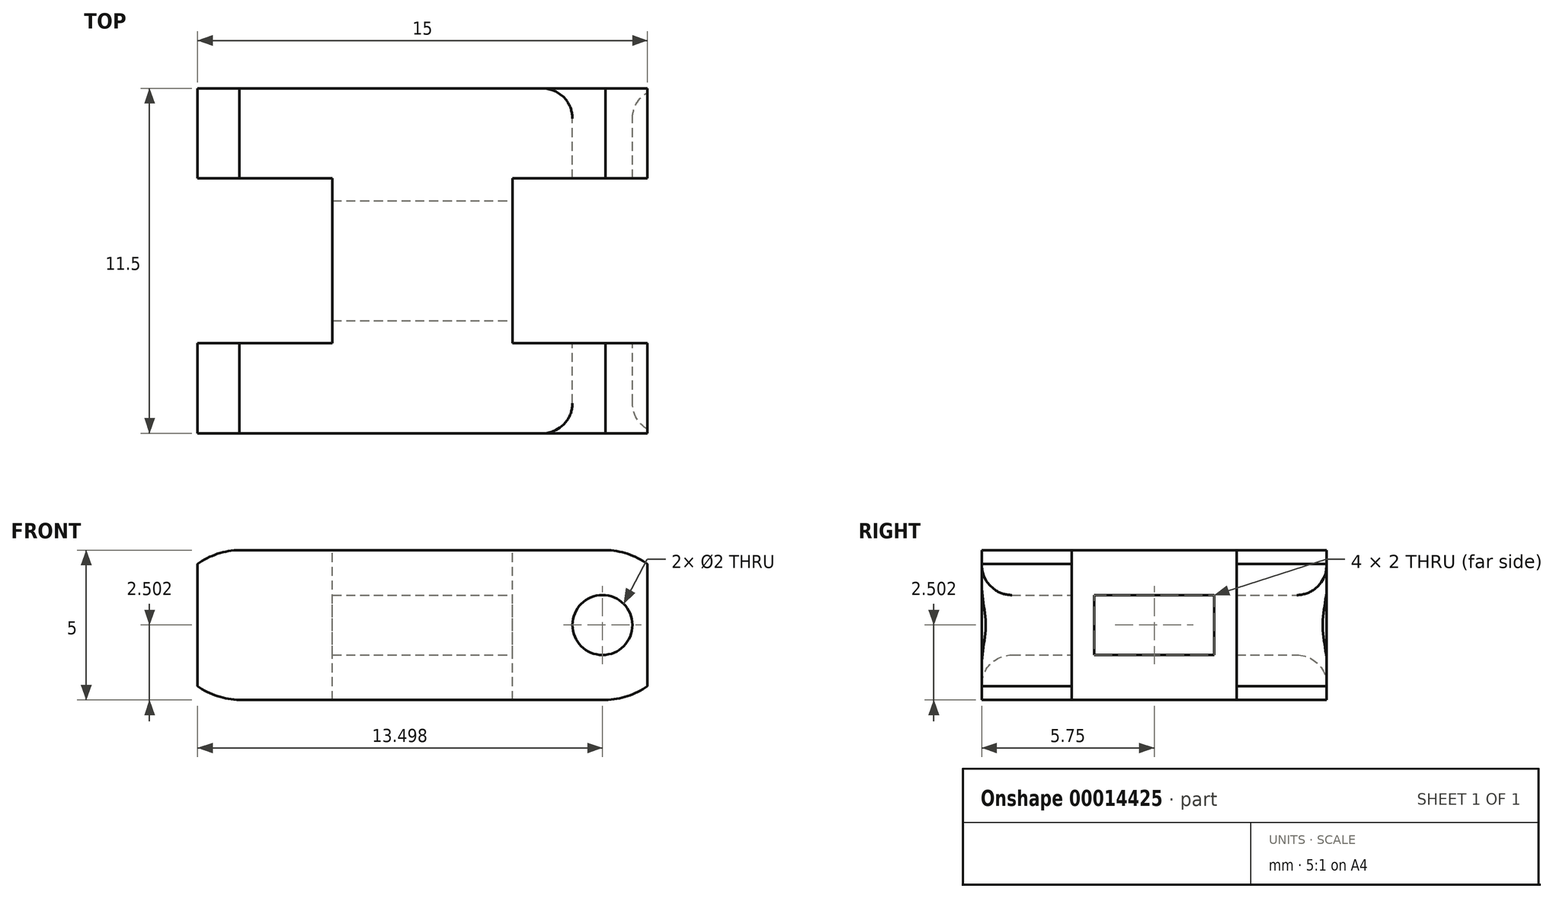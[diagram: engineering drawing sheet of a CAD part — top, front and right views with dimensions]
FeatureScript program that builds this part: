
annotation { "Feature Type Name" : "Feature", "Feature Type Description" : "" }
export const myFeature = defineFeature(function(context is Context, id is Id, definition is map)
    precondition{}
    {
        {
            var Q0;
            Q0=qCreatedBy(makeId("Front.planeOp"),FACE);
            var sketch = newSketch(context, id + "F0", { "sketchPlane" : qUnion([Q0])});
            skLineSegment(sketch, "E0.bottom", {"start": v(28.09, 13.2) * mm, "end": v(43.09, 13.2) * mm});
            skLineSegment(sketch, "E0.top", {"start": v(28.09, 8.2) * mm, "end": v(43.09, 8.2) * mm});
            skLineSegment(sketch, "E0.left", {"start": v(28.09, 13.2) * mm, "end": v(28.09, 8.2) * mm});
            skLineSegment(sketch, "E0.right", {"start": v(43.09, 13.2) * mm, "end": v(43.09, 8.2) * mm});
            skLineSegment(sketch, "E1", {"start": v(35.59, 8.2) * mm, "end": v(35.59, 13.2) * mm, "construction": true});
            skPoint(sketch, "E2", {"position": v(31.09, 13.2) * mm});
            skLineSegment(sketch, "E3", {"start": v(28.09, 8.2) * mm, "end": v(31.09, 13.2) * mm, "construction": true});
            skLineSegment(sketch, "E4", {"start": v(31.09, 13.2) * mm, "end": v(31.09, 8.2) * mm, "construction": true});
            skLineSegment(sketch, "E5", {"start": v(31.09, 8.2) * mm, "end": v(28.09, 13.2) * mm, "construction": true});
            skCircle(sketch, "E6", {"center": v(29.59, 10.7) * mm, "radius": 1 * mm});
            skLineSegment(sketch, "E7", {"start": v(29.59, 13.2) * mm, "end": v(29.59, 8.2) * mm, "construction": true});
            skLineSegment(sketch, "E8", {"start": v(28.09, 10.7) * mm, "end": v(31.09, 10.7) * mm, "construction": true});
            skArc(sketch, "E9", {"start": v(29.59, 13.2) * mm, "mid": v(27.04, 10.7) * mm, "end": v(29.59, 8.2) * mm});
            skCircle(sketch, "E10.0.MirrorC", {"center": v(41.59, 10.7) * mm, "radius": 1 * mm});
            skArc(sketch, "E11.0.MirrorCS", {"start": v(41.59, 13.2) * mm, "mid": v(44.14, 10.7) * mm, "end": v(41.59, 8.2) * mm});
            skSolve(sketch);
        }
        {
            var Q0;
            {var subQ5=sQuery(id+"F0.wireOp",EDGE,"E0.right");Q0=makeQuery(id+"F0.imprint","IMPRINT",FACE,{"disambiguationData":[TD([[makeQuery(id+"F0.imprint","IMPRINT",EDGE,{"derivedFrom":subQ5}),-1.0]])]});}
            var Q1;
            Q1=makeQuery(id+"F0.imprint","IMPRINT",FACE,{"disambiguationData":[TD([[makeQuery(id+"F0.imprint","IMPRINT",EDGE,{"derivedFrom":sQuery(id+"F0.wireOp",EDGE,"E6")}),-1.0]])]});
            var Q2;
            {var subQ5=sQuery(id+"F0.wireOp",EDGE,"E0.left");Q2=makeQuery(id+"F0.imprint","IMPRINT",FACE,{"disambiguationData":[TD([[makeQuery(id+"F0.imprint","IMPRINT",EDGE,{"derivedFrom":subQ5}),1.0]])]});}
            var Q3;
            Q3=makeQuery(id+"F0.imprint","IMPRINT",FACE,{"disambiguationData":[TD([[makeQuery(id+"F0.imprint","IMPRINT",EDGE,{"derivedFrom":sQuery(id+"F0.wireOp",EDGE,"E6")}),1.0]])]});
            var Q4;
            Q4=makeQuery(id+"F0.imprint","IMPRINT",FACE,{"disambiguationData":[TD([[makeQuery(id+"F0.imprint","IMPRINT",EDGE,{"derivedFrom":sQuery(id+"F0.wireOp",EDGE,"E10.0.MirrorC")}),-1.0]])]});
            extrude(context, id + "F1", {"entities" : qUnion([Q0, Q1, Q2, Q3, Q4]), "depth" : 9.5 * mm});
        }
        {
            var Q0;
            Q0=makeQuery(id+"F1.opExtrude","SWEPT_FACE",FACE,{"disambiguationData":[OSD([sQuery(id+"F0.wireOp",EDGE,"E0.bottom")])]});
            var sketch = newSketch(context, id + "F2", { "sketchPlane" : qUnion([Q0])});
            skLineSegment(sketch, "E12", {"start": v(35.59, 0) * mm, "end": v(35.59, -9.5) * mm, "construction": true});
            skLineSegment(sketch, "E13", {"start": v(28.09, -4.75) * mm, "end": v(43.09, -4.75) * mm, "construction": true});
            skPoint(sketch, "E14", {"position": v(32.59, 0) * mm});
            skLineSegment(sketch, "E15", {"start": v(32.59, 0) * mm, "end": v(32.59, -9.5) * mm, "construction": true});
            skPoint(sketch, "E16", {"position": v(28.09, -2) * mm});
            skLineSegment(sketch, "E17", {"start": v(28.09, -2) * mm, "end": v(32.59, -2) * mm});
            skLineSegment(sketch, "E18.0.MirrorCS", {"start": v(28.09, -7.5) * mm, "end": v(32.59, -7.5) * mm});
            skLineSegment(sketch, "E19", {"start": v(32.59, -7.5) * mm, "end": v(32.59, -2) * mm});
            skLineSegment(sketch, "E20", {"start": v(28.09, -2) * mm, "end": v(28.09, -7.5) * mm});
            skLineSegment(sketch, "E21.MirrorCS", {"start": v(38.59, -7.5) * mm, "end": v(38.59, -2) * mm});
            skLineSegment(sketch, "E22.MirrorCS", {"start": v(43.09, -2) * mm, "end": v(38.59, -2) * mm});
            skLineSegment(sketch, "E23.MirrorCS", {"start": v(43.09, -2) * mm, "end": v(43.09, -7.5) * mm});
            skLineSegment(sketch, "E24.MirrorCS", {"start": v(43.09, -7.5) * mm, "end": v(38.59, -7.5) * mm});
            skSolve(sketch);
        }
        {
            var Q0;
            Q0=makeQuery(id+"F2.imprint","IMPRINT",FACE,{"disambiguationData":[TD([[makeQuery(id+"F2.imprint","IMPRINT",EDGE,{"derivedFrom":sQuery(id+"F2.wireOp",EDGE,"E17")}),-1.0]])]});
            var Q1;
            Q1=makeQuery(id+"F2.imprint","IMPRINT",FACE,{"disambiguationData":[TD([[makeQuery(id+"F2.imprint","IMPRINT",EDGE,{"derivedFrom":sQuery(id+"F2.wireOp",EDGE,"8c34fa15-d911-4d8d-b620-4605c3a337e2.0.MirrorCS")}),-1.0]])]});
            var Q2;
            Q2=makeQuery(id+"F2.imprint","IMPRINT",FACE,{"disambiguationData":[TD([[makeQuery(id+"F2.imprint","IMPRINT",EDGE,{"derivedFrom":sQuery(id+"F2.wireOp",EDGE,"E21.MirrorCS")}),-1.0]])]});
            extrude(context, id + "F3", {"entities" : qUnion([Q0, Q1, Q2]), "operationType" : NewBodyOperationType.REMOVE, "endBound" : BoundingType.THROUGH_ALL, "oppositeDirection" : true, "depth" : 25 * mm});
        }
        {
            var Q0;
            {var subQ5=sQuery(id+"F0.wireOp",EDGE,"E0.right");Q0=makeQuery(id+"F0.imprint","IMPRINT",FACE,{"disambiguationData":[TD([[makeQuery(id+"F0.imprint","IMPRINT",EDGE,{"derivedFrom":subQ5}),-1.0]])]});}
            var Q1;
            {var subQ5=sQuery(id+"F0.wireOp",EDGE,"E0.left");Q1=makeQuery(id+"F0.imprint","IMPRINT",FACE,{"disambiguationData":[TD([[makeQuery(id+"F0.imprint","IMPRINT",EDGE,{"derivedFrom":subQ5}),1.0]])]});}
            extrude(context, id + "F4", {"entities" : qUnion([Q0, Q1]), "operationType" : NewBodyOperationType.REMOVE, "endBound" : BoundingType.THROUGH_ALL, "depth" : 25 * mm});
        }
        {
            var Q0;
            Q0=makeQuery(id+"F0.imprint","IMPRINT",FACE,{"disambiguationData":[TD([[makeQuery(id+"F0.imprint","IMPRINT",EDGE,{"derivedFrom":sQuery(id+"F0.wireOp",EDGE,"E6")}),1.0]])]});
            var Q1;
            Q1=makeQuery(id+"F0.imprint","IMPRINT",FACE,{"disambiguationData":[TD([[makeQuery(id+"F0.imprint","IMPRINT",EDGE,{"derivedFrom":sQuery(id+"F0.wireOp",EDGE,"E10.0.MirrorC")}),-1.0]])]});
            extrude(context, id + "F5", {"entities" : qUnion([Q0, Q1]), "operationType" : NewBodyOperationType.ADD, "oppositeDirection" : true, "depth" : 1 * mm});
        }
        {
            var Q0;
            Q0=makeQuery(id+"F1.opExtrude","CAP_FACE",FACE,{"disambiguationData":[OSD([sQuery(id+"F0.wireOp",EDGE,"E0.bottom"),sQuery(id+"F0.wireOp",EDGE,"E0.top"),sQuery(id+"F0.wireOp",EDGE,"E0.left"),sQuery(id+"F0.wireOp",EDGE,"E0.right")])],"isStart":false});
            var sketch = newSketch(context, id + "F6", { "sketchPlane" : qUnion([Q0])});
            skLineSegment(sketch, "E25", {"start": v(35.59, 8.2) * mm, "end": v(35.59, 13.2) * mm, "construction": true});
            skPoint(sketch, "E26", {"position": v(31.09, 8.2) * mm});
            skPoint(sketch, "E27", {"position": v(28.09, 8.2) * mm});
            skLineSegment(sketch, "E28", {"start": v(31.09, 8.2) * mm, "end": v(31.09, 13.2) * mm, "construction": true});
            skLineSegment(sketch, "E29", {"start": v(31.09, 13.2) * mm, "end": v(28.09, 8.2) * mm, "construction": true});
            skPoint(sketch, "E30", {"position": v(28.09, 13.2) * mm});
            skLineSegment(sketch, "E31", {"start": v(28.09, 13.2) * mm, "end": v(28.09, 8.2) * mm, "construction": true});
            skLineSegment(sketch, "E32", {"start": v(31.09, 13.2) * mm, "end": v(28.09, 13.2) * mm, "construction": true});
            skLineSegment(sketch, "E33", {"start": v(28.09, 13.2) * mm, "end": v(31.09, 8.2) * mm, "construction": true});
            skCircle(sketch, "E34", {"center": v(29.59, 10.7) * mm, "radius": 1 * mm});
            skCircle(sketch, "E35.MirrorC", {"center": v(41.59, 10.7) * mm, "radius": 1 * mm});
            skPoint(sketch, "E36", {"position": v(35.59, 8.2) * mm});
            skCircle(sketch, "E37.MirrorC", {"center": v(41.59, 10.7) * mm, "radius": 1 * mm, "construction": true});
            skSolve(sketch);
        }
        {
            var Q0;
            Q0=makeQuery(id+"F6.imprint","IMPRINT",FACE,{"disambiguationData":[TD([[makeQuery(id+"F6.imprint","IMPRINT",EDGE,{"derivedFrom":sQuery(id+"F6.wireOp",EDGE,"E34")}),1.0]])]});
            var Q1;
            Q1=makeQuery(id+"F6.imprint","IMPRINT",FACE,{"disambiguationData":[TD([[makeQuery(id+"F6.imprint","IMPRINT",EDGE,{"derivedFrom":sQuery(id+"F6.wireOp",EDGE,"E35.MirrorC")}),-1.0]])]});
            extrude(context, id + "F7", {"entities" : qUnion([Q0, Q1]), "operationType" : NewBodyOperationType.ADD, "depth" : 1 * mm});
        }
        {
            var Q0;
            Q0=makeQuery(id+"F3.boolean.opBoolean","COPY",FACE,{"derivedFrom":makeQuery(id+"F3.opExtrude","SWEPT_FACE",FACE,{"disambiguationData":[OSD([sQuery(id+"F2.wireOp",EDGE,"E21.MirrorCS")])]})});
            var sketch = newSketch(context, id + "F8", { "sketchPlane" : qUnion([Q0])});
            skPoint(sketch, "E38", {"position": v(-4.75, 13.2) * mm});
            skPoint(sketch, "E39", {"position": v(-4.75, 8.2) * mm});
            skLineSegment(sketch, "E40", {"start": v(-4.75, 13.2) * mm, "end": v(-4.75, 8.2) * mm, "construction": true});
            skPoint(sketch, "E41", {"position": v(-4.75, 10.7) * mm});
            skLineSegment(sketch, "E42", {"start": v(-7.5, 10.7) * mm, "end": v(-2, 10.7) * mm, "construction": true});
            skPoint(sketch, "E43", {"position": v(-6.75, 10.7) * mm});
            skPoint(sketch, "E44", {"position": v(-2.75, 10.7) * mm});
            skPoint(sketch, "E45", {"position": v(-4.75, 11.7) * mm});
            skPoint(sketch, "E46", {"position": v(-4.75, 9.7) * mm});
            skLineSegment(sketch, "E47", {"start": v(-6.75, 10.7) * mm, "end": v(-6.75, 11.7) * mm, "construction": true});
            skLineSegment(sketch, "E48", {"start": v(-6.75, 11.7) * mm, "end": v(-4.75, 11.7) * mm});
            skLineSegment(sketch, "E49", {"start": v(-6.75, 10.7) * mm, "end": v(-6.75, 11.7) * mm});
            skLineSegment(sketch, "E50.MirrorCS", {"start": v(-6.75, 9.7) * mm, "end": v(-4.75, 9.7) * mm});
            skLineSegment(sketch, "E51.MirrorCS", {"start": v(-6.75, 10.7) * mm, "end": v(-6.75, 9.7) * mm});
            skLineSegment(sketch, "E52.MirrorCS", {"start": v(-2.75, 11.7) * mm, "end": v(-4.75, 11.7) * mm});
            skLineSegment(sketch, "E53.MirrorCS", {"start": v(-2.75, 10.7) * mm, "end": v(-2.75, 11.7) * mm});
            skLineSegment(sketch, "E54.MirrorCS", {"start": v(-2.75, 10.7) * mm, "end": v(-2.75, 9.7) * mm});
            skLineSegment(sketch, "E55.MirrorCS", {"start": v(-2.75, 9.7) * mm, "end": v(-4.75, 9.7) * mm});
            skSolve(sketch);
        }
        {
            var Q0;
            Q0=makeQuery(id+"F8.imprint","IMPRINT",FACE,{"disambiguationData":[TD([[makeQuery(id+"F8.imprint","IMPRINT",EDGE,{"derivedFrom":sQuery(id+"F8.wireOp",EDGE,"E48")}),-1.0]])]});
            extrude(context, id + "F9", {"entities" : qUnion([Q0]), "operationType" : NewBodyOperationType.REMOVE, "endBound" : BoundingType.THROUGH_ALL, "oppositeDirection" : true, "depth" : 25 * mm});
        }
        {
            var Q0;
            Q0=makeQuery(id+"F7.opExtrude","CAP_EDGE",EDGE,{"disambiguationData":[OSD([sQuery(id+"F6.wireOp",EDGE,"E34")])],"isStart":false});
            var Q1;
            Q1=makeQuery(id+"F7.opExtrude","CAP_EDGE",EDGE,{"disambiguationData":[OSD([sQuery(id+"F6.wireOp",EDGE,"E35.MirrorC")])],"isStart":false});
            var Q2;
            Q2=makeQuery(id+"F5.opExtrude","CAP_EDGE",EDGE,{"disambiguationData":[OSD([sQuery(id+"F0.wireOp",EDGE,"E6")])],"isStart":false});
            var Q3;
            Q3=makeQuery(id+"F5.opExtrude","CAP_EDGE",EDGE,{"disambiguationData":[OSD([sQuery(id+"F0.wireOp",EDGE,"E10.0.MirrorC")])],"isStart":false});
            fillet(context, id + "F10", {"entities" : qUnion([Q0, Q1, Q2, Q3]), "radius" : 1 * mm, "tangentPropagation" : true, "allowEdgeOverflow" : false});
        }
    });
